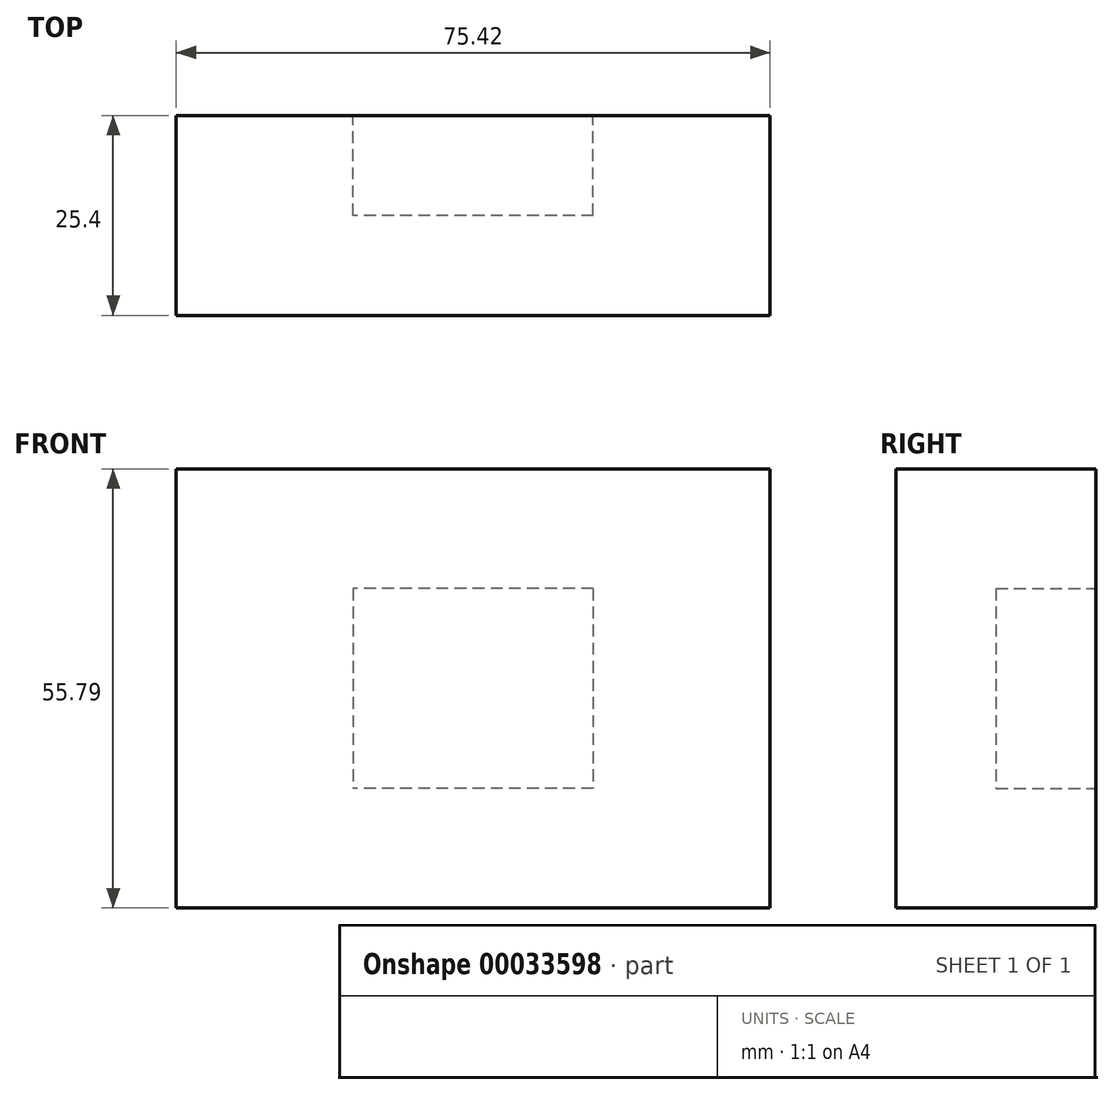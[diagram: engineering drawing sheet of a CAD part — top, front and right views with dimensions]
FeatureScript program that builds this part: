
annotation { "Feature Type Name" : "Feature", "Feature Type Description" : "" }
export const myFeature = defineFeature(function(context is Context, id is Id, definition is map)
    precondition{}
    {
        {
            var Q0;
            Q0=qCreatedBy(makeId("Front.planeOp"),FACE);
            var sketch = newSketch(context, id + "F0", { "sketchPlane" : qUnion([Q0])});
            skLineSegment(sketch, "E0.bottom", {"start": v(-62.08, 67.42) * mm, "end": v(13.34, 67.42) * mm});
            skLineSegment(sketch, "E0.top", {"start": v(-62.08, 11.63) * mm, "end": v(13.34, 11.63) * mm});
            skLineSegment(sketch, "E0.left", {"start": v(-62.08, 67.42) * mm, "end": v(-62.08, 11.63) * mm});
            skLineSegment(sketch, "E0.right", {"start": v(13.34, 67.42) * mm, "end": v(13.34, 11.63) * mm});
            skSolve(sketch);
        }
        {
            var Q0;
            Q0 = qSketchRegion(id + "F0", true);
            extrude(context, id + "F1", {"entities" : qUnion([Q0]), "depth" : 25.4 * mm});
        }
        {
            var Q0;
            Q0=makeQuery(id+"F1.opExtrude","CAP_FACE",FACE,{"disambiguationData":[OSD([sQuery(id+"F0.wireOp",EDGE,"E0.bottom"),sQuery(id+"F0.wireOp",EDGE,"E0.top"),sQuery(id+"F0.wireOp",EDGE,"E0.left"),sQuery(id+"F0.wireOp",EDGE,"E0.right")])],"isStart":true});
            var sketch = newSketch(context, id + "F2", { "sketchPlane" : qUnion([Q0])});
            skLineSegment(sketch, "E1.bottom", {"start": v(9.13, 52.23) * mm, "end": v(39.61, 52.23) * mm});
            skLineSegment(sketch, "E1.top", {"start": v(9.13, 26.83) * mm, "end": v(39.61, 26.83) * mm});
            skLineSegment(sketch, "E1.left", {"start": v(9.13, 52.23) * mm, "end": v(9.13, 26.83) * mm});
            skLineSegment(sketch, "E1.right", {"start": v(39.61, 52.23) * mm, "end": v(39.61, 26.83) * mm});
            skSolve(sketch);
        }
        {
            var Q0;
            Q0 = qSketchRegion(id + "F2", true);
            extrude(context, id + "F3", {"entities" : qUnion([Q0]), "operationType" : NewBodyOperationType.REMOVE, "oppositeDirection" : true, "depth" : 12.7 * mm});
        }
    });
